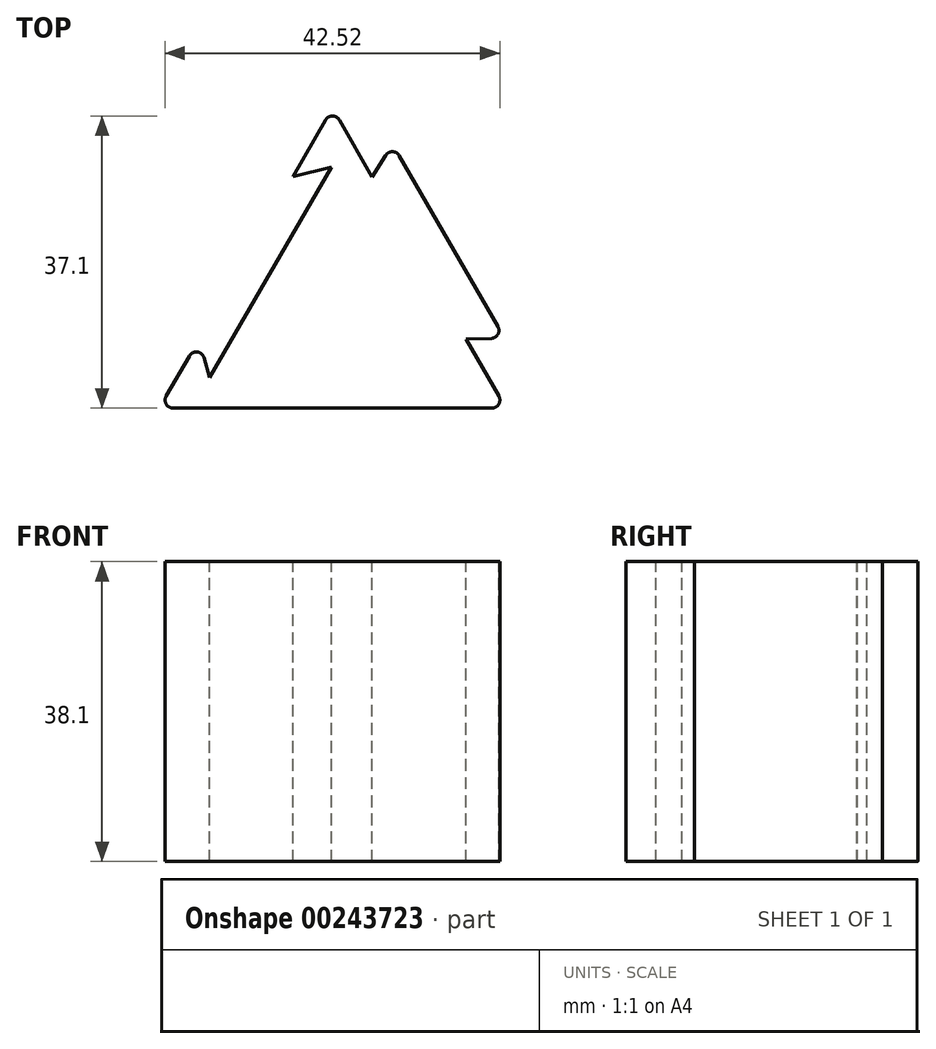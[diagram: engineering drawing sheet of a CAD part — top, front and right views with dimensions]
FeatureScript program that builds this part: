
annotation { "Feature Type Name" : "Feature", "Feature Type Description" : "" }
export const myFeature = defineFeature(function(context is Context, id is Id, definition is map)
    precondition{}
    {
        {
            var Q0;
            Q0=qCreatedBy(makeId("Top.planeOp"),FACE);
            var sketch = newSketch(context, id + "F0", { "sketchPlane" : qUnion([Q0])});
            skLineSegment(sketch, "E0", {"start": v(0, 38.1) * mm, "end": v(-22, 0) * mm});
            skLineSegment(sketch, "E1", {"start": v(-22, 0) * mm, "end": v(22, 0) * mm});
            skLineSegment(sketch, "E2", {"start": v(22, 0) * mm, "end": v(0, 38.1) * mm});
            skSolve(sketch);
        }
        {
            var Q0;
            Q0 = qSketchRegion(id + "F0", true);
            extrude(context, id + "F1", {"entities" : qUnion([Q0]), "depth" : 38.1 * mm});
        }
        {
            var Q0;
            Q0=makeQuery(id+"F1.opExtrude","CAP_FACE",FACE,{"disambiguationData":[OSD([sQuery(id+"F0.wireOp",EDGE,"E0"),sQuery(id+"F0.wireOp",EDGE,"E1"),sQuery(id+"F0.wireOp",EDGE,"E2")])],"isStart":false});
            var sketch = newSketch(context, id + "F2", { "sketchPlane" : qUnion([Q0])});
            skLineSegment(sketch, "E3", {"start": v(-5, 29.44) * mm, "end": v(-17, 8.66) * mm});
            skLineSegment(sketch, "E4", {"start": v(-17, 8.66) * mm, "end": v(-15.6, 3.86) * mm});
            skLineSegment(sketch, "E5", {"start": v(-15.6, 3.86) * mm, "end": v(-0.14, 30.63) * mm});
            skLineSegment(sketch, "E6", {"start": v(-0.14, 30.63) * mm, "end": v(-5, 29.44) * mm});
            skSolve(sketch);
        }
        {
            var Q0;
            Q0 = qSketchRegion(id + "F2", true);
            extrude(context, id + "F3", {"entities" : qUnion([Q0]), "operationType" : NewBodyOperationType.REMOVE, "endBound" : BoundingType.THROUGH_ALL, "oppositeDirection" : true, "depth" : 25 * mm});
        }
        {
            var Q0;
            Q0=makeQuery(id+"F3.boolean.opBoolean","COPY",EDGE,{"derivedFrom":makeQuery(id+"F3.opExtrude","SWEPT_EDGE",EDGE,{"disambiguationData":[OSD([sQuery(id+"F0.wireOp",EDGE,"E0"),sQuery(id+"F2.wireOp",EDGE,"E3"),sQuery(id+"F2.wireOp",EDGE,"E6")])]})});
            var Q1;
            Q1=makeQuery(id+"F3.boolean.opBoolean","COPY",EDGE,{"derivedFrom":makeQuery(id+"F3.opExtrude","SWEPT_EDGE",EDGE,{"disambiguationData":[OSD([sQuery(id+"F0.wireOp",EDGE,"E0"),sQuery(id+"F2.wireOp",EDGE,"E3"),sQuery(id+"F2.wireOp",EDGE,"E4")])]})});
            fillet(context, id + "F4", {"entities" : qUnion([Q0, Q1]), "radius" : 1 * mm, "tangentPropagation" : true, "allowEdgeOverflow" : false});
        }
        {
            var Q0;
            Q0=makeQuery(id+"F1.opExtrude","CAP_FACE",FACE,{"disambiguationData":[OSD([sQuery(id+"F0.wireOp",EDGE,"E0"),sQuery(id+"F0.wireOp",EDGE,"E1"),sQuery(id+"F0.wireOp",EDGE,"E2")])],"isStart":false});
            var sketch = newSketch(context, id + "F5", { "sketchPlane" : qUnion([Q0])});
            skLineSegment(sketch, "E7", {"start": v(5.05, 29.35) * mm, "end": v(7.64, 33.51) * mm});
            skLineSegment(sketch, "E8", {"start": v(7.64, 33.51) * mm, "end": v(21.84, 8.9) * mm});
            skLineSegment(sketch, "E9", {"start": v(21.84, 8.9) * mm, "end": v(16.95, 8.75) * mm});
            skLineSegment(sketch, "E10", {"start": v(5.05, 29.35) * mm, "end": v(17.42, 7.92) * mm});
            skSolve(sketch);
        }
        {
            var Q0;
            Q0 = qSketchRegion(id + "F5", true);
            var Q1;
            Q1=makeQuery(id+"F1.opExtrude","CAP_FACE",FACE,{"disambiguationData":[OSD([sQuery(id+"F0.wireOp",EDGE,"E0"),sQuery(id+"F0.wireOp",EDGE,"E1"),sQuery(id+"F0.wireOp",EDGE,"E2")])],"isStart":true});
            extrude(context, id + "F6", {"entities" : qUnion([Q0]), "operationType" : NewBodyOperationType.ADD, "endBound" : BoundingType.UP_TO_SURFACE, "oppositeDirection" : true, "endBoundEntityFace" : qUnion([Q1]), "depth" : 25 * mm});
        }
        {
            var Q0;
            Q0=makeQuery(id+"F6.opExtrude","SWEPT_EDGE",EDGE,{"disambiguationData":[OSD([sQuery(id+"F5.wireOp",EDGE,"E7"),sQuery(id+"F5.wireOp",EDGE,"E8")])]});
            var Q1;
            Q1=makeQuery(id+"F6.opExtrude","SWEPT_EDGE",EDGE,{"disambiguationData":[OSD([sQuery(id+"F5.wireOp",EDGE,"E8"),sQuery(id+"F5.wireOp",EDGE,"E9")])]});
            fillet(context, id + "F7", {"entities" : qUnion([Q0, Q1]), "radius" : 1 * mm, "tangentPropagation" : true, "allowEdgeOverflow" : false});
        }
        {
            var Q0;
            Q0=makeQuery(id+"F1.opExtrude","SWEPT_EDGE",EDGE,{"disambiguationData":[OSD([sQuery(id+"F0.wireOp",EDGE,"E0"),sQuery(id+"F0.wireOp",EDGE,"E2")])]});
            var Q1;
            Q1=makeQuery(id+"F1.opExtrude","SWEPT_EDGE",EDGE,{"disambiguationData":[OSD([sQuery(id+"F0.wireOp",EDGE,"E0"),sQuery(id+"F0.wireOp",EDGE,"E1")])]});
            var Q2;
            Q2=makeQuery(id+"F1.opExtrude","SWEPT_EDGE",EDGE,{"disambiguationData":[OSD([sQuery(id+"F0.wireOp",EDGE,"E1"),sQuery(id+"F0.wireOp",EDGE,"E2")])]});
            fillet(context, id + "F8", {"entities" : qUnion([Q0, Q1, Q2]), "radius" : 1 * mm, "tangentPropagation" : true, "allowEdgeOverflow" : false});
        }
    });
